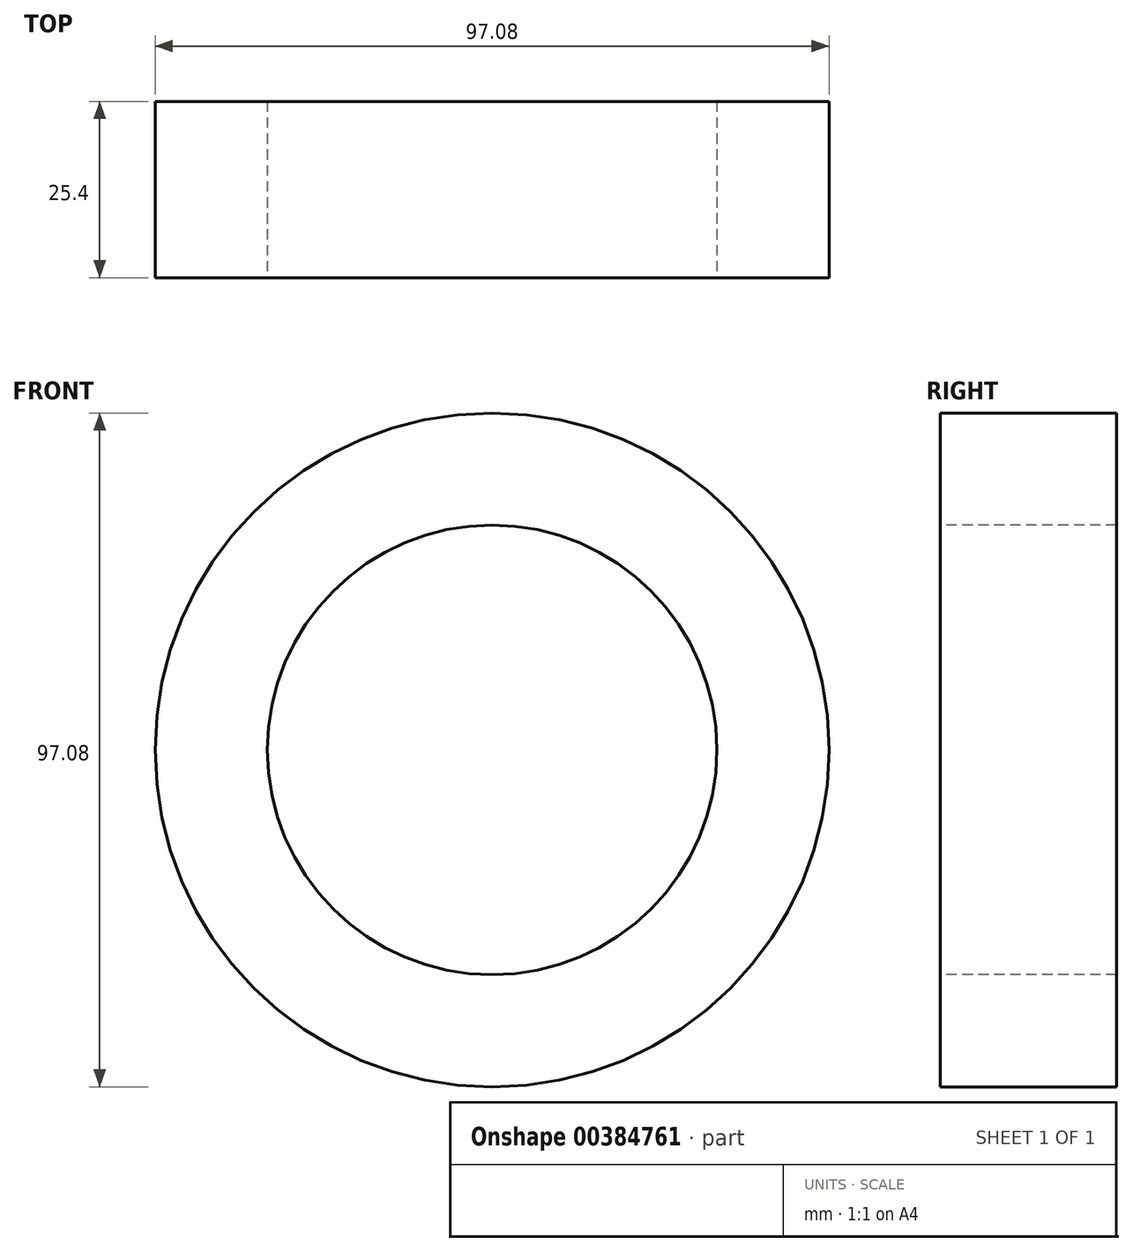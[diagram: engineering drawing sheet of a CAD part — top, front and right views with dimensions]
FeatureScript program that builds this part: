
annotation { "Feature Type Name" : "Feature", "Feature Type Description" : "" }
export const myFeature = defineFeature(function(context is Context, id is Id, definition is map)
    precondition{}
    {
        {
            var Q0;
            Q0=qCreatedBy(makeId("Front.planeOp"),FACE);
            var sketch = newSketch(context, id + "F0", { "sketchPlane" : qUnion([Q0])});
            skCircle(sketch, "E0", {"center": v(0, 0) * mm, "radius": 48.54 * mm});
            skCircle(sketch, "E1", {"center": v(0, 0) * mm, "radius": 32.39 * mm});
            skSolve(sketch);
        }
        {
            var Q0;
            Q0=sQuery(id+"F0.wireOp",EDGE,"E0");
            var Q1;
            Q1=sQuery(id+"F0.wireOp",EDGE,"E1");
            extrude(context, id + "F1", {"bodyType" : ToolBodyType.SURFACE, "surfaceEntities" : qUnion([Q0, Q1]), "depth" : 25.4 * mm});
        }
    });
